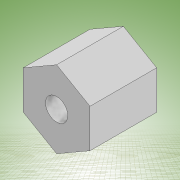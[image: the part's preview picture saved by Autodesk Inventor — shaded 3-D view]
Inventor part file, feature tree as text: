
AUTODESK INVENTOR PART (.ipt)
format: ipt  version: 2022 (Build 260153000, 153)  size: 109,568 bytes
history: native  units: mm
features: other x1, extrude x1, sketch x1
ambient origin geometry x8: Origin, YZ Plane, XZ Plane, XY Plane, X Axis, Y Axis, Z Axis, Center Point
bodies: Body1 (feature_tree)
feature tree (3):
  other  "Sólido1"
  extrude  "Extrusión1"  Depth=6.0mm
  sketch  "Boceto1"  dims[d0=6.0mm d1=2.0mm d2=6.0mm d3=0.0mm]
